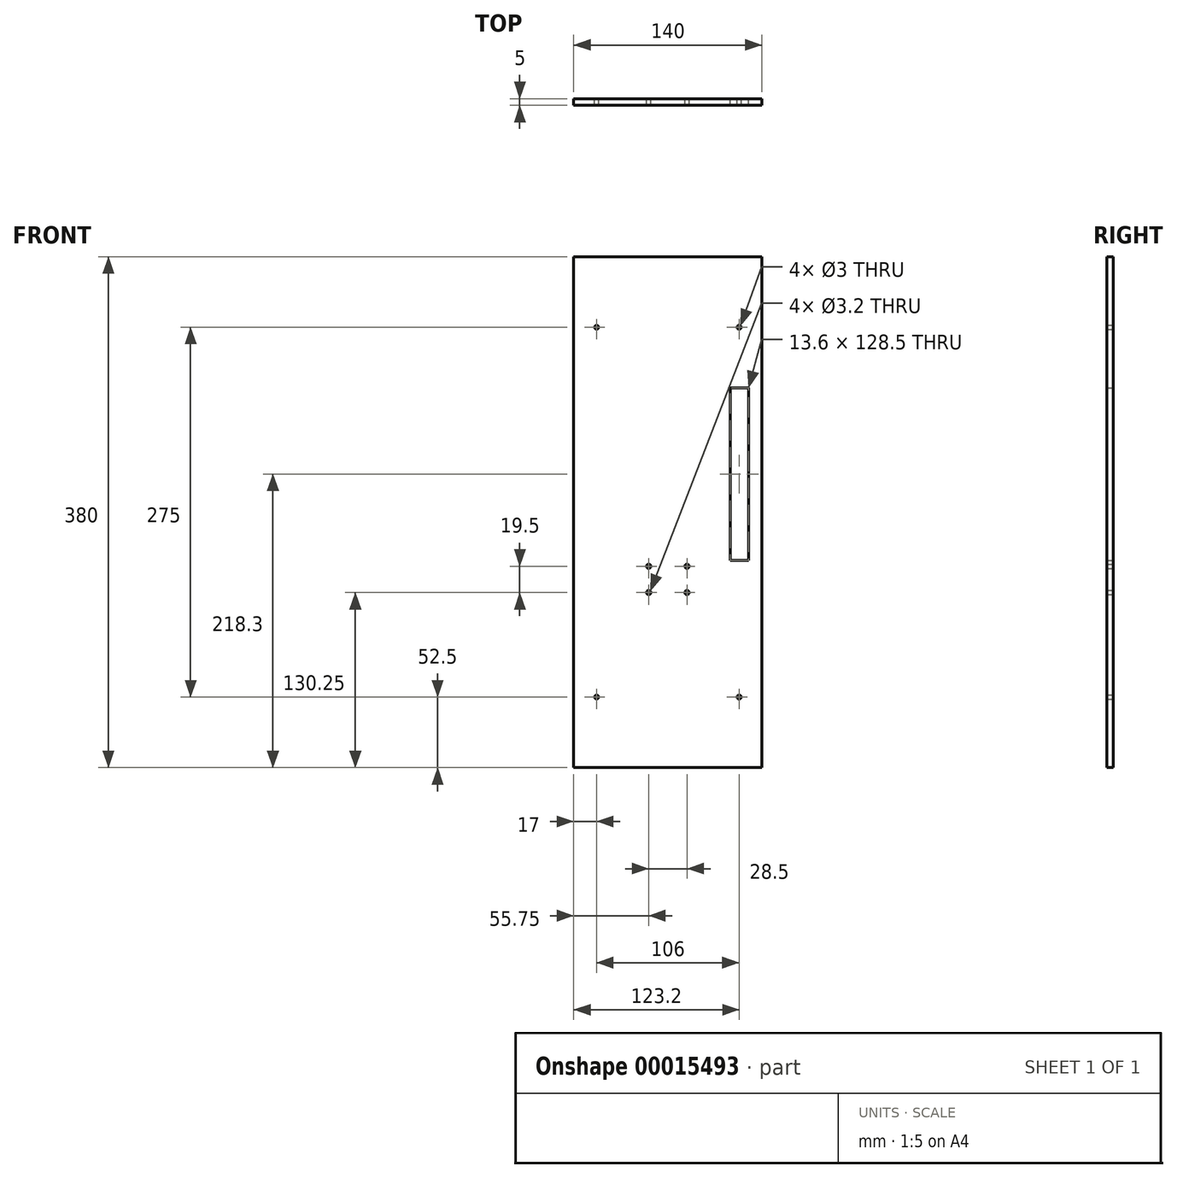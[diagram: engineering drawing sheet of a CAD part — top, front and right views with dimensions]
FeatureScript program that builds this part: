
annotation { "Feature Type Name" : "Feature", "Feature Type Description" : "" }
export const myFeature = defineFeature(function(context is Context, id is Id, definition is map)
    precondition{}
    {
        {
            var Q0;
            Q0=qCreatedBy(makeId("Front.planeOp"),FACE);
            var sketch = newSketch(context, id + "F0", { "sketchPlane" : qUnion([Q0])});
            skLineSegment(sketch, "E0.rect.bottom", {"start": v(70, 190) * mm, "end": v(-70, 190) * mm});
            skLineSegment(sketch, "E0.rect.top", {"start": v(70, -190) * mm, "end": v(-70, -190) * mm});
            skLineSegment(sketch, "E0.rect.left", {"start": v(70, 190) * mm, "end": v(70, -190) * mm});
            skLineSegment(sketch, "E0.rect.right", {"start": v(-70, 190) * mm, "end": v(-70, -190) * mm});
            skPoint(sketch, "E0.rect.middle", {"position": v(0, 0) * mm});
            skSolve(sketch);
        }
        {
            var Q0;
            Q0 = qSketchRegion(id + "F0", true);
            extrude(context, id + "F1", {"entities" : qUnion([Q0]), "depth" : 5 * mm});
        }
        {
            var Q0;
            Q0=qCreatedBy(makeId("Front.planeOp"),FACE);
            var sketch = newSketch(context, id + "F2", { "sketchPlane" : qUnion([Q0])});
            skCircle(sketch, "E1", {"center": v(-53, 137.5) * mm, "radius": 1.5 * mm});
            skLineSegment(sketch, "E2.rect.bottom", {"start": v(-53, 137.5) * mm, "end": v(53, 137.5) * mm, "construction": true});
            skLineSegment(sketch, "E2.rect.top", {"start": v(-53, -137.5) * mm, "end": v(53, -137.5) * mm, "construction": true});
            skLineSegment(sketch, "E2.rect.left", {"start": v(-53, 137.5) * mm, "end": v(-53, -137.5) * mm, "construction": true});
            skLineSegment(sketch, "E2.rect.right", {"start": v(53, 137.5) * mm, "end": v(53, -137.5) * mm, "construction": true});
            skPoint(sketch, "E2.rect.middle", {"position": v(0, 0) * mm});
            skCircle(sketch, "E3", {"center": v(53, 137.5) * mm, "radius": 1.5 * mm});
            skCircle(sketch, "E4", {"center": v(53, -137.5) * mm, "radius": 1.5 * mm});
            skCircle(sketch, "E5", {"center": v(-53, -137.5) * mm, "radius": 1.5 * mm});
            skSolve(sketch);
        }
        {
            var Q0;
            Q0 = qSketchRegion(id + "F2", true);
            extrude(context, id + "F3", {"entities" : qUnion([Q0]), "operationType" : NewBodyOperationType.REMOVE, "endBound" : BoundingType.THROUGH_ALL, "depth" : 25 * mm});
        }
        {
            var Q0;
            Q0=qCreatedBy(makeId("Front.planeOp"),FACE);
            var sketch = newSketch(context, id + "F4", { "sketchPlane" : qUnion([Q0])});
            skLineSegment(sketch, "E6.rect.bottom", {"start": v(60, 92.55) * mm, "end": v(46.4, 92.55) * mm});
            skLineSegment(sketch, "E6.rect.top", {"start": v(60, -35.95) * mm, "end": v(46.4, -35.95) * mm});
            skLineSegment(sketch, "E6.rect.left", {"start": v(60, 92.55) * mm, "end": v(60, -35.95) * mm});
            skLineSegment(sketch, "E6.rect.right", {"start": v(46.4, 92.55) * mm, "end": v(46.4, -35.95) * mm});
            skPoint(sketch, "E6.rect.middle", {"position": v(53.2, 28.3) * mm});
            skSolve(sketch);
        }
        {
            var Q0;
            Q0 = qSketchRegion(id + "F4", true);
            extrude(context, id + "F5", {"entities" : qUnion([Q0]), "operationType" : NewBodyOperationType.REMOVE, "endBound" : BoundingType.THROUGH_ALL, "depth" : 25 * mm});
        }
        {
            var Q0;
            Q0=qCreatedBy(makeId("Front.planeOp"),FACE);
            var Q1;
            Q1=qCreatedBy(makeId("Front.planeOp"),FACE);
            var Q2;
            Q2=qCreatedBy(makeId("Front.planeOp"),FACE);
            var sketch = newSketch(context, id + "F6", { "sketchPlane" : qUnion([Q0, Q1, Q2])});
            skLineSegment(sketch, "E7.bottom", {"start": v(14.25, -40.25) * mm, "end": v(-14.25, -40.25) * mm, "construction": true});
            skLineSegment(sketch, "E7.top", {"start": v(14.25, -59.75) * mm, "end": v(-14.25, -59.75) * mm, "construction": true});
            skLineSegment(sketch, "E7.left", {"start": v(14.25, -40.25) * mm, "end": v(14.25, -59.75) * mm, "construction": true});
            skLineSegment(sketch, "E7.right", {"start": v(-14.25, -40.25) * mm, "end": v(-14.25, -59.75) * mm, "construction": true});
            skLineSegment(sketch, "E8", {"start": v(0, 0) * mm, "end": v(0, -40.25) * mm, "construction": true});
            skPoint(sketch, "E9", {"position": v(-14.25, -59.75) * mm});
            skPoint(sketch, "E10", {"position": v(14.25, -59.75) * mm});
            skPoint(sketch, "E11", {"position": v(14.25, -40.25) * mm});
            skPoint(sketch, "E12", {"position": v(-14.25, -40.25) * mm});
            skLineSegment(sketch, "E13", {"start": v(14.25, -50) * mm, "end": v(-14.25, -50) * mm, "construction": true});
            skSolve(sketch);
        }
        {
            var Q0;
            Q0=sQuery(id+"F6.wireOp",VERTEX,"E11");
            var Q1;
            Q1=sQuery(id+"F6.wireOp",VERTEX,"E10");
            var Q2;
            Q2=sQuery(id+"F6.wireOp",VERTEX,"E9");
            var Q3;
            Q3=sQuery(id+"F6.wireOp",VERTEX,"E12");
            var Q4;
            Q4=sQuery(id+"F6.wireOp",VERTEX,"E11");
            var Q5;
            Q5=sQuery(id+"F6.wireOp",VERTEX,"E10");
            var Q6;
            Q6=sQuery(id+"F6.wireOp",VERTEX,"E9");
            var Q7;
            Q7=sQuery(id+"F6.wireOp",VERTEX,"E12");
            var Q8;
            Q8=makeQuery(id+"F1.opExtrude","SWEPT_BODY",BODY,{"disambiguationData":[OSD([sQuery(id+"F0.wireOp",EDGE,"E0.rect.bottom"),sQuery(id+"F0.wireOp",EDGE,"E0.rect.top"),sQuery(id+"F0.wireOp",EDGE,"E0.rect.left"),sQuery(id+"F0.wireOp",EDGE,"E0.rect.right")])]});
            var Q9;
            Q9=makeQuery(id+"F1.opExtrude","SWEPT_BODY",BODY,{"disambiguationData":[OSD([sQuery(id+"F0.wireOp",EDGE,"E0.rect.bottom"),sQuery(id+"F0.wireOp",EDGE,"E0.rect.top"),sQuery(id+"F0.wireOp",EDGE,"E0.rect.left"),sQuery(id+"F0.wireOp",EDGE,"E0.rect.right")])]});
            hole(context, id + "F7", {"style" : HoleStyle.SIMPLE, "endStyle" : HoleEndStyle.THROUGH, "oppositeDirection" : true, "standardTappedOrClearance" : lookupTablePath({ "standard" : "ISO", "size" : "3.2", "type" : "Drilled" }), "standardBlindInLast" : lookupTablePath({ "standard" : "ISO", "size" : "3.2", "type" : "Drilled" }), "holeDiameter" : 3.2 * mm, "locations" : qUnion([Q0, Q1, Q2, Q3, Q4, Q5, Q6, Q7]), "scope" : qUnion([Q8, Q9]), "isTappedThrough" : true});
        }
    });
